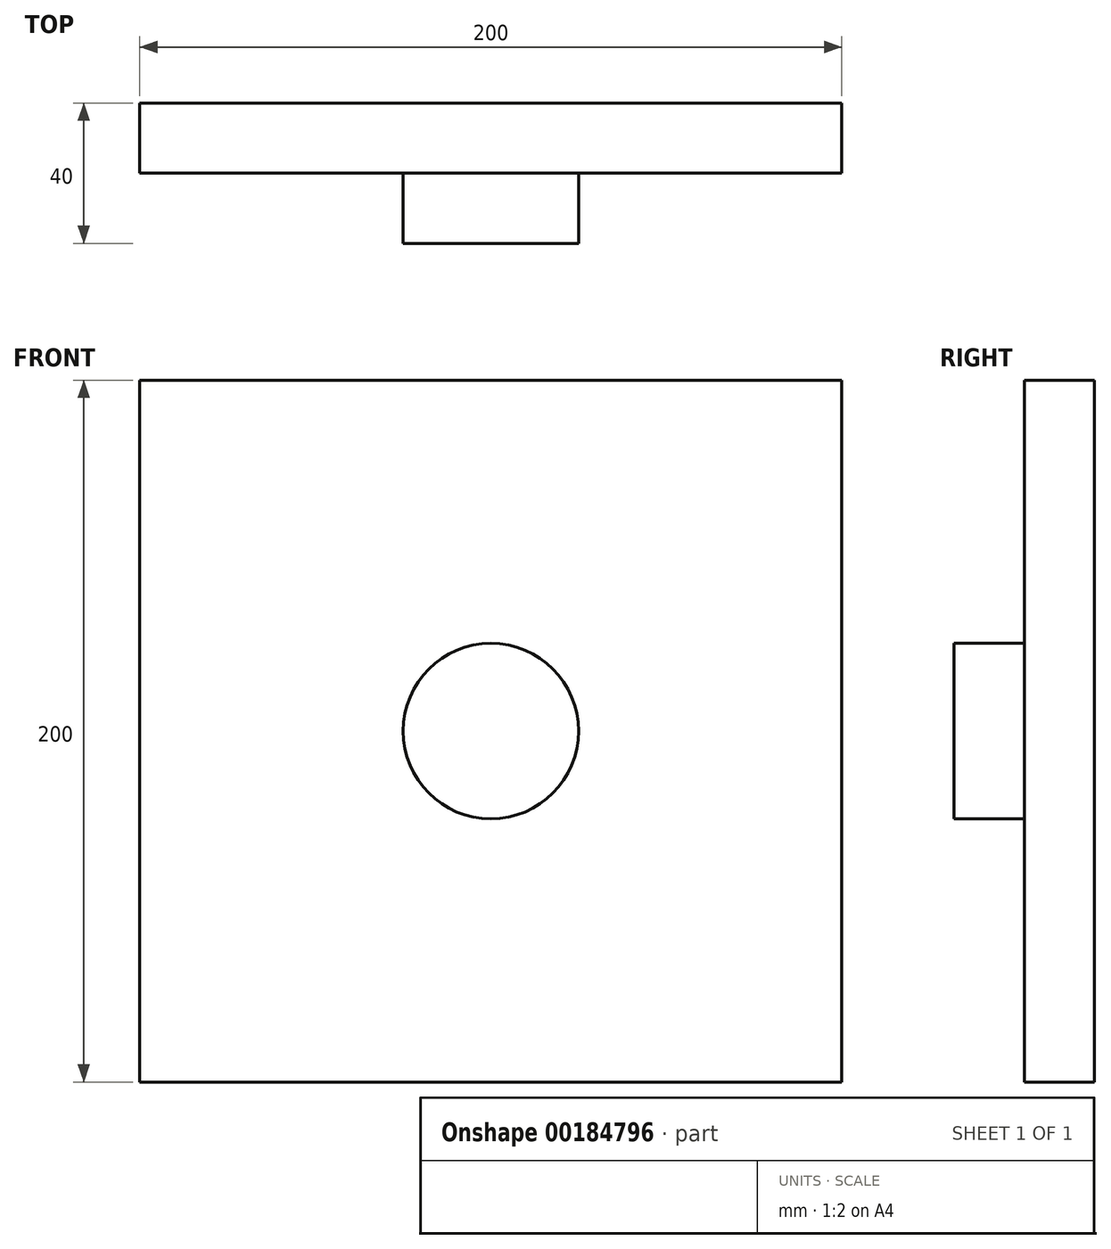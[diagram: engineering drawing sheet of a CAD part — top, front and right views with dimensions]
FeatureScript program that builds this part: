
annotation { "Feature Type Name" : "Feature", "Feature Type Description" : "" }
export const myFeature = defineFeature(function(context is Context, id is Id, definition is map)
    precondition{}
    {
        {
            var Q0;
            Q0=qCreatedBy(makeId("Front.planeOp"),FACE);
            var sketch = newSketch(context, id + "F0", { "sketchPlane" : qUnion([Q0])});
            skLineSegment(sketch, "E0.bottom", {"start": v(0, 0) * mm, "end": v(200, 0) * mm});
            skLineSegment(sketch, "E0.top", {"start": v(0, 200) * mm, "end": v(200, 200) * mm});
            skLineSegment(sketch, "E0.left", {"start": v(0, 0) * mm, "end": v(0, 200) * mm});
            skLineSegment(sketch, "E0.right", {"start": v(200, 0) * mm, "end": v(200, 200) * mm});
            skSolve(sketch);
        }
        {
            var Q0;
            Q0=makeQuery(id+"F0.imprint","IMPRINT",FACE,{"disambiguationData":[TD([[makeQuery(id+"F0.imprint","IMPRINT",EDGE,{"derivedFrom":sQuery(id+"F0.wireOp",EDGE,"E0.bottom")}),1.0]])]});
            extrude(context, id + "F1", {"entities" : qUnion([Q0]), "depth" : 20 * mm});
        }
        {
            var Q0;
            Q0=makeQuery(id+"F1.opExtrude","CAP_FACE",FACE,{"disambiguationData":[OSD([sQuery(id+"F0.wireOp",EDGE,"E0.bottom"),sQuery(id+"F0.wireOp",EDGE,"E0.top"),sQuery(id+"F0.wireOp",EDGE,"E0.left"),sQuery(id+"F0.wireOp",EDGE,"E0.right")])],"isStart":false});
            var sketch = newSketch(context, id + "F2", { "sketchPlane" : qUnion([Q0])});
            skLineSegment(sketch, "E1", {"start": v(0, 100) * mm, "end": v(200, 100) * mm, "construction": true});
            skLineSegment(sketch, "E2", {"start": v(100, 200) * mm, "end": v(100, 0) * mm, "construction": true});
            skCircle(sketch, "E3", {"center": v(100, 100) * mm, "radius": 25 * mm});
            skSolve(sketch);
        }
        {
            var Q0;
            Q0=makeQuery(id+"F2.imprint","IMPRINT",FACE,{"disambiguationData":[TD([[makeQuery(id+"F2.imprint","IMPRINT",EDGE,{"derivedFrom":sQuery(id+"F2.wireOp",EDGE,"E3")}),1.0]])]});
            extrude(context, id + "F3", {"entities" : qUnion([Q0]), "operationType" : NewBodyOperationType.ADD, "depth" : 20 * mm});
        }
    });
